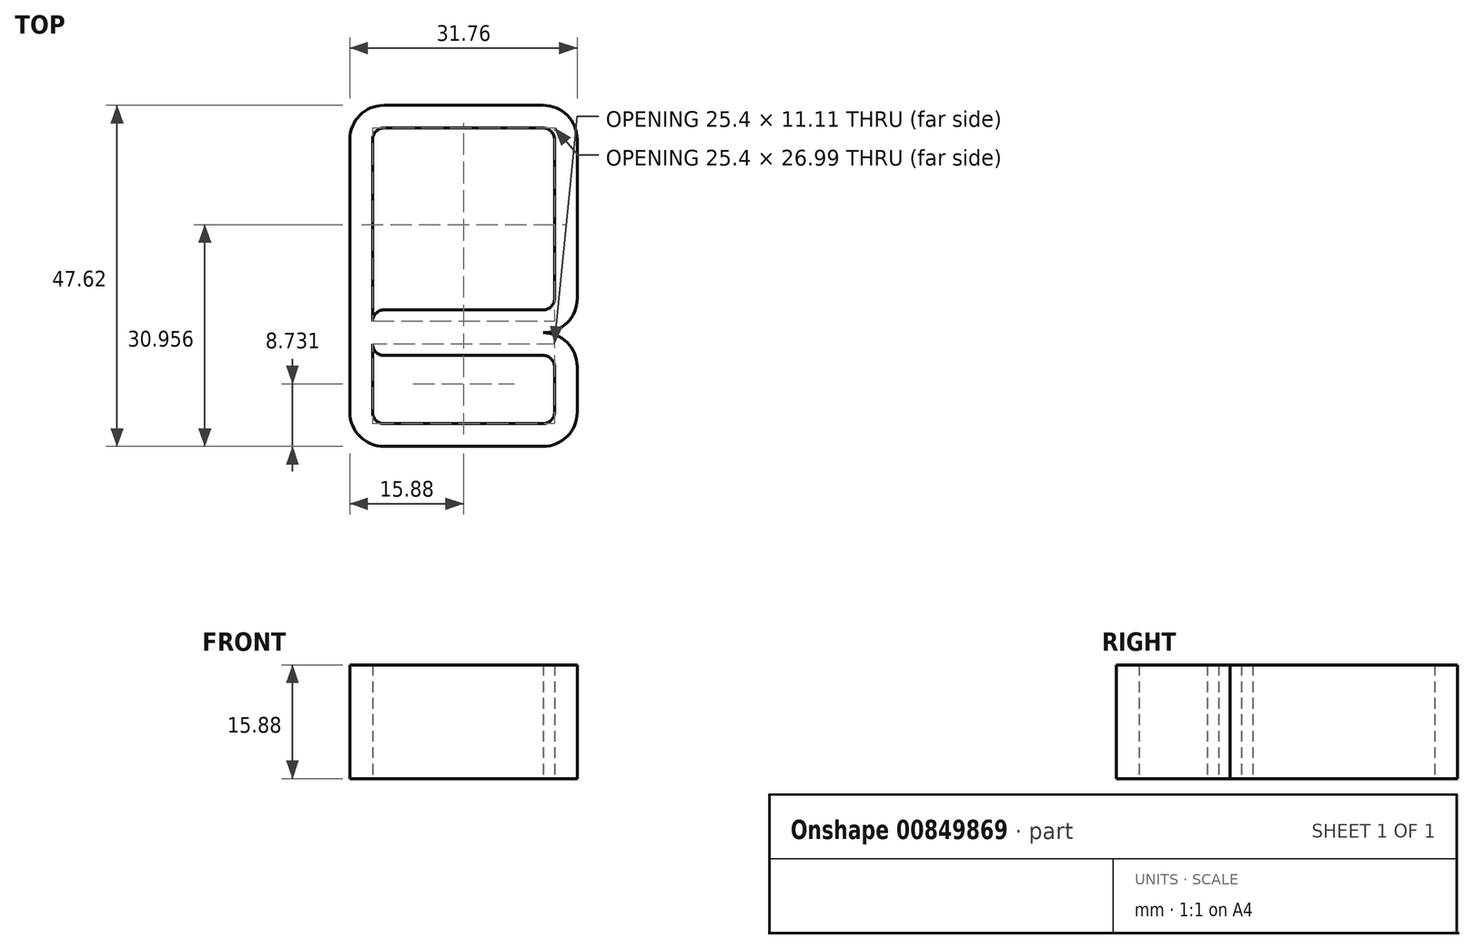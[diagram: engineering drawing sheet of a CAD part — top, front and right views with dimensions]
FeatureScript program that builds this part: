
annotation { "Feature Type Name" : "Feature", "Feature Type Description" : "" }
export const myFeature = defineFeature(function(context is Context, id is Id, definition is map)
    precondition{}
    {
        {
            var Q0;
            Q0=qCreatedBy(makeId("Top.planeOp"),FACE);
            var sketch = newSketch(context, id + "F0", { "sketchPlane" : qUnion([Q0])});
            skLineSegment(sketch, "E0.bottom", {"start": v(11.11, -19.05) * mm, "end": v(-11.11, -19.05) * mm});
            skLineSegment(sketch, "E0.left", {"start": v(15.87, -14.29) * mm, "end": v(15.87, -7.94) * mm});
            skLineSegment(sketch, "E0.right", {"start": v(-15.88, -14.29) * mm, "end": v(-15.87, 19.05) * mm});
            skPoint(sketch, "E0.middle", {"position": v(0, 0) * mm});
            skLineSegment(sketch, "E1.bottom", {"start": v(11.11, 0) * mm, "end": v(-11.11, 0) * mm});
            skLineSegment(sketch, "E1.top", {"start": v(11.11, 25.4) * mm, "end": v(-11.11, 25.4) * mm});
            skLineSegment(sketch, "E1.left", {"start": v(12.7, 1.59) * mm, "end": v(12.7, 23.81) * mm});
            skLineSegment(sketch, "E1.right", {"start": v(-12.7, 0) * mm, "end": v(-12.7, 23.81) * mm});
            skPoint(sketch, "E1.middle", {"position": v(0, 12.7) * mm});
            skLineSegment(sketch, "E2.bottom", {"start": v(-11.11, -6.35) * mm, "end": v(11.11, -6.35) * mm});
            skLineSegment(sketch, "E2.top", {"start": v(-11.11, -15.88) * mm, "end": v(11.11, -15.88) * mm});
            skLineSegment(sketch, "E2.left", {"start": v(-12.7, -6.35) * mm, "end": v(-12.7, -14.29) * mm});
            skLineSegment(sketch, "E2.right", {"start": v(12.7, -7.94) * mm, "end": v(12.7, -14.29) * mm});
            skLineSegment(sketch, "E3", {"start": v(-11.11, -3.18) * mm, "end": v(11.11, -3.17) * mm});
            skLineSegment(sketch, "E4", {"start": v(-12.7, -1.59) * mm, "end": v(-12.7, -1.59) * mm});
            skLineSegment(sketch, "E5", {"start": v(-12.7, -4.76) * mm, "end": v(-12.7, -4.76) * mm});
            skLineSegment(sketch, "E6", {"start": v(-15.87, 19.05) * mm, "end": v(-15.87, 23.81) * mm});
            skLineSegment(sketch, "E7", {"start": v(-11.11, 28.58) * mm, "end": v(11.11, 28.57) * mm});
            skLineSegment(sketch, "E8", {"start": v(15.88, 23.81) * mm, "end": v(15.88, 19.05) * mm});
            skPoint(sketch, "E9.visualSharp", {"position": v(-12.7, -15.88) * mm});
            skArc(sketch, "E9.filletArc", {"start": v(-12.7, -14.29) * mm, "mid": v(-12.24, -15.41) * mm, "end": v(-11.11, -15.88) * mm});
            skPoint(sketch, "E10.visualSharp", {"position": v(12.7, -15.88) * mm});
            skArc(sketch, "E10.filletArc", {"start": v(11.11, -15.88) * mm, "mid": v(12.24, -15.41) * mm, "end": v(12.7, -14.29) * mm});
            skPoint(sketch, "E11.visualSharp", {"position": v(12.7, -6.35) * mm});
            skArc(sketch, "E11.filletArc", {"start": v(12.7, -7.94) * mm, "mid": v(12.24, -6.81) * mm, "end": v(11.11, -6.35) * mm});
            skPoint(sketch, "E12.visualSharp", {"position": v(12.7, 0) * mm});
            skArc(sketch, "E12.filletArc", {"start": v(11.11, 0) * mm, "mid": v(12.24, 0.46) * mm, "end": v(12.7, 1.59) * mm});
            skPoint(sketch, "E13.visualSharp", {"position": v(12.7, 25.4) * mm});
            skArc(sketch, "E13.filletArc", {"start": v(12.7, 23.81) * mm, "mid": v(12.24, 24.94) * mm, "end": v(11.11, 25.4) * mm});
            skPoint(sketch, "E14.visualSharp", {"position": v(-12.7, 25.4) * mm});
            skArc(sketch, "E14.filletArc", {"start": v(-11.11, 25.4) * mm, "mid": v(-12.24, 24.94) * mm, "end": v(-12.7, 23.81) * mm});
            skPoint(sketch, "E15.visualSharp", {"position": v(-12.7, 0) * mm});
            skArc(sketch, "E15.filletArc", {"start": v(-11.11, 0) * mm, "mid": v(-12.24, -0.46) * mm, "end": v(-12.7, -1.59) * mm});
            skPoint(sketch, "E16.visualSharp", {"position": v(-12.7, -3.18) * mm});
            skArc(sketch, "E16.filletArc", {"start": v(-12.7, -1.59) * mm, "mid": v(-12.24, -2.71) * mm, "end": v(-11.11, -3.18) * mm});
            skLineSegment(sketch, "E17", {"start": v(-11.11, -3.18) * mm, "end": v(-11.11, -3.18) * mm});
            skArc(sketch, "E18.filletArc", {"start": v(-11.11, -3.18) * mm, "mid": v(-12.24, -3.64) * mm, "end": v(-12.7, -4.76) * mm});
            skPoint(sketch, "E19.visualSharp", {"position": v(-12.7, -6.35) * mm});
            skArc(sketch, "E19.filletArc", {"start": v(-12.7, -4.76) * mm, "mid": v(-12.24, -5.89) * mm, "end": v(-11.11, -6.35) * mm});
            skLineSegment(sketch, "E20", {"start": v(-12.7, 0) * mm, "end": v(-12.7, -6.35) * mm});
            skPoint(sketch, "E21.visualSharp", {"position": v(-15.87, 28.58) * mm});
            skArc(sketch, "E21.filletArc", {"start": v(-11.11, 28.58) * mm, "mid": v(-14.48, 27.18) * mm, "end": v(-15.87, 23.81) * mm});
            skPoint(sketch, "E22.visualSharp", {"position": v(-15.88, -19.05) * mm});
            skArc(sketch, "E22.filletArc", {"start": v(-15.88, -14.29) * mm, "mid": v(-14.48, -17.66) * mm, "end": v(-11.11, -19.05) * mm});
            skPoint(sketch, "E23.visualSharp", {"position": v(15.87, -19.05) * mm});
            skArc(sketch, "E23.filletArc", {"start": v(11.11, -19.05) * mm, "mid": v(14.48, -17.66) * mm, "end": v(15.87, -14.29) * mm});
            skPoint(sketch, "E24.newPointB", {"position": v(15.88, 19.05) * mm});
            skArc(sketch, "E24.filletArc", {"start": v(15.87, -7.94) * mm, "mid": v(14.48, -4.57) * mm, "end": v(11.11, -3.17) * mm});
            skLineSegment(sketch, "E25", {"start": v(15.88, 19.05) * mm, "end": v(15.88, 1.59) * mm});
            skLineSegment(sketch, "E26", {"start": v(11.11, -3.17) * mm, "end": v(11.11, -3.17) * mm});
            skPoint(sketch, "E27.visualSharp", {"position": v(15.87, -3.17) * mm});
            skArc(sketch, "E27.filletArc", {"start": v(11.11, -3.17) * mm, "mid": v(14.48, -1.78) * mm, "end": v(15.88, 1.59) * mm});
            skPoint(sketch, "E28.visualSharp", {"position": v(15.88, 28.58) * mm});
            skArc(sketch, "E28.filletArc", {"start": v(15.88, 23.81) * mm, "mid": v(14.48, 27.18) * mm, "end": v(11.11, 28.57) * mm});
            skLineSegment(sketch, "E29", {"start": v(-11.11, -3.18) * mm, "end": v(-12.7, -3.18) * mm});
            skSolve(sketch);
        }
        {
            var Q0;
            Q0=makeQuery(id+"F0.imprint","IMPRINT",FACE,{"disambiguationData":[TD([[makeQuery(id+"F0.imprint","IMPRINT",EDGE,{"derivedFrom":sQuery(id+"F0.wireOp",EDGE,"E0.bottom")}),-1.0]])]});
            var Q1;
            {var subQ0=sQuery(id+"F0.wireOp",EDGE,"E16.filletArc");Q1=makeQuery(id+"F0.imprint","IMPRINT",FACE,{"disambiguationData":[TD([[makeQuery(id+"F0.imprint","IMPRINT",EDGE,{"derivedFrom":subQ0}),-1.0]])]});}
            var Q2;
            {var subQ0=sQuery(id+"F0.wireOp",EDGE,"E18.filletArc");Q2=makeQuery(id+"F0.imprint","IMPRINT",FACE,{"disambiguationData":[TD([[makeQuery(id+"F0.imprint","IMPRINT",EDGE,{"derivedFrom":subQ0}),-1.0]])]});}
            extrude(context, id + "F1", {"entities" : qUnion([Q0, Q1, Q2]), "depth" : 15.88 * mm, "offsetDistance" : 25.4 * mm});
        }
        {
            var Q0;
            Q0=sQuery(id+"F0.wireOp",EDGE,"E3");
            var Q1;
            Q1=sQuery(id+"F0.wireOp",EDGE,"E20");
            extrude(context, id + "F2", {"bodyType" : ToolBodyType.SURFACE, "surfaceEntities" : qUnion([Q0, Q1]), "depth" : 15.88 * mm, "offsetDistance" : 25.4 * mm});
        }
        {
            var Q0;
            Q0=sQuery(id+"F0.wireOp",EDGE,"E29");
            extrude(context, id + "F3", {"bodyType" : ToolBodyType.SURFACE, "surfaceEntities" : qUnion([Q0]), "depth" : 15.88 * mm, "offsetDistance" : 25.4 * mm});
        }
    });
